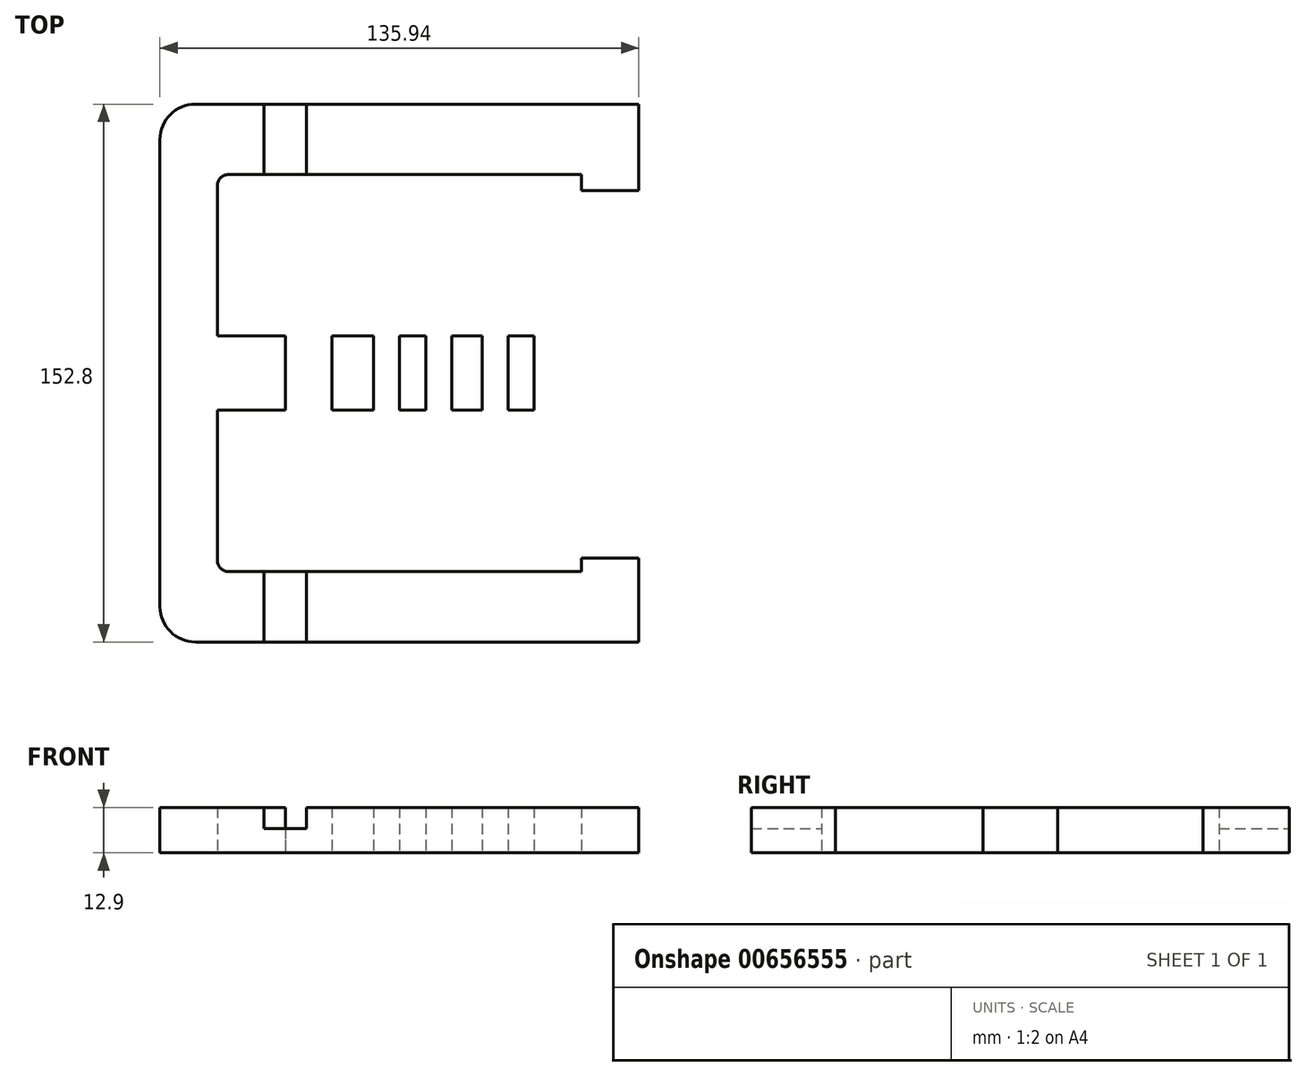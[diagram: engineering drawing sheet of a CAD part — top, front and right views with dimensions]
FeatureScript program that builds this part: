
annotation { "Feature Type Name" : "Feature", "Feature Type Description" : "" }
export const myFeature = defineFeature(function(context is Context, id is Id, definition is map)
    precondition{}
    {
        {
            var Q0;
            Q0=qCreatedBy(makeId("Top.planeOp"),FACE);
            var sketch = newSketch(context, id + "F0", { "sketchPlane" : qUnion([Q0])});
            skLineSegment(sketch, "E0.bottom", {"start": v(-57.93, -76.4) * mm, "end": v(67.97, -76.4) * mm});
            skLineSegment(sketch, "E0.top", {"start": v(-57.93, 76.4) * mm, "end": v(67.97, 76.4) * mm});
            skLineSegment(sketch, "E0.left", {"start": v(-67.97, -66.35) * mm, "end": v(-67.97, 66.35) * mm});
            skLineSegment(sketch, "E0.right", {"start": v(67.97, -76.4) * mm, "end": v(67.97, 76.4) * mm});
            skPoint(sketch, "E0.middle", {"position": v(0, 0) * mm});
            skLineSegment(sketch, "E1.bottom", {"start": v(-48.5, -56.4) * mm, "end": v(51.68, -56.4) * mm});
            skLineSegment(sketch, "E1.top", {"start": v(-48.5, 56.4) * mm, "end": v(51.68, 56.4) * mm});
            skLineSegment(sketch, "E1.left", {"start": v(-51.68, -53.23) * mm, "end": v(-51.68, -10.56) * mm});
            skLineSegment(sketch, "E1.right", {"start": v(51.68, -56.4) * mm, "end": v(51.68, -10.56) * mm});
            skLineSegment(sketch, "E2.bottom", {"start": v(-51.68, -10.56) * mm, "end": v(51.68, -10.56) * mm});
            skLineSegment(sketch, "E2.top", {"start": v(-51.68, 10.56) * mm, "end": v(51.68, 10.56) * mm});
            skLineSegment(sketch, "E3.trimOffspring", {"start": v(-51.68, 10.56) * mm, "end": v(-51.68, 53.23) * mm});
            skLineSegment(sketch, "E4.trimOffspring", {"start": v(51.68, 10.56) * mm, "end": v(51.68, 56.4) * mm});
            skLineSegment(sketch, "E5", {"start": v(-38.44, 76.4) * mm, "end": v(-38.44, 56.4) * mm});
            skLineSegment(sketch, "E6", {"start": v(-26.4, 76.4) * mm, "end": v(-26.4, 56.4) * mm});
            skLineSegment(sketch, "E7", {"start": v(-26.4, -56.4) * mm, "end": v(-26.4, -76.4) * mm});
            skLineSegment(sketch, "E8", {"start": v(-38.44, -56.4) * mm, "end": v(-38.44, -76.4) * mm});
            skLineSegment(sketch, "E9", {"start": v(67.97, 51.87) * mm, "end": v(51.68, 51.87) * mm});
            skLineSegment(sketch, "E10", {"start": v(51.68, 51.87) * mm, "end": v(67.97, 51.87) * mm});
            skLineSegment(sketch, "E11", {"start": v(67.97, -52.52) * mm, "end": v(51.68, -52.52) * mm});
            skLineSegment(sketch, "E12.bottom", {"start": v(-32.37, 10.56) * mm, "end": v(-19.14, 10.56) * mm});
            skLineSegment(sketch, "E12.top", {"start": v(-32.37, -10.56) * mm, "end": v(-19.14, -10.56) * mm});
            skLineSegment(sketch, "E12.left", {"start": v(-32.37, 10.56) * mm, "end": v(-32.37, -10.56) * mm});
            skLineSegment(sketch, "E12.right", {"start": v(-19.14, 10.56) * mm, "end": v(-19.14, -10.56) * mm});
            skLineSegment(sketch, "E13.bottom", {"start": v(-7.39, 10.56) * mm, "end": v(0, 10.56) * mm});
            skLineSegment(sketch, "E13.top", {"start": v(-7.39, -10.56) * mm, "end": v(0, -10.56) * mm});
            skLineSegment(sketch, "E13.left", {"start": v(-7.39, 10.56) * mm, "end": v(-7.39, -10.56) * mm});
            skLineSegment(sketch, "E13.right", {"start": v(0, 10.56) * mm, "end": v(0, -10.56) * mm});
            skLineSegment(sketch, "E14.bottom", {"start": v(7.5, 10.56) * mm, "end": v(14.88, 10.56) * mm});
            skLineSegment(sketch, "E14.top", {"start": v(7.5, -10.56) * mm, "end": v(14.88, -10.56) * mm});
            skLineSegment(sketch, "E14.left", {"start": v(7.5, 10.56) * mm, "end": v(7.5, -10.56) * mm});
            skLineSegment(sketch, "E14.right", {"start": v(14.88, 10.56) * mm, "end": v(14.88, -10.56) * mm});
            skLineSegment(sketch, "E15.bottom", {"start": v(23.47, 10.56) * mm, "end": v(30.86, 10.56) * mm});
            skLineSegment(sketch, "E15.top", {"start": v(23.47, -10.56) * mm, "end": v(30.86, -10.56) * mm});
            skLineSegment(sketch, "E15.left", {"start": v(23.47, 10.56) * mm, "end": v(23.47, -10.56) * mm});
            skLineSegment(sketch, "E15.right", {"start": v(30.86, 10.56) * mm, "end": v(30.86, -10.56) * mm});
            skLineSegment(sketch, "E16.bottom", {"start": v(38.24, 10.56) * mm, "end": v(45.28, 10.56) * mm});
            skLineSegment(sketch, "E16.top", {"start": v(38.24, -10.56) * mm, "end": v(45.28, -10.56) * mm});
            skLineSegment(sketch, "E16.left", {"start": v(38.24, 10.56) * mm, "end": v(38.24, -10.56) * mm});
            skLineSegment(sketch, "E16.right", {"start": v(45.28, 10.56) * mm, "end": v(45.28, -10.56) * mm});
            skPoint(sketch, "E17.visualSharp", {"position": v(-51.68, 56.4) * mm});
            skArc(sketch, "E17.filletArc", {"start": v(-48.5, 56.4) * mm, "mid": v(-50.75, 55.47) * mm, "end": v(-51.68, 53.23) * mm});
            skPoint(sketch, "E18.visualSharp", {"position": v(-67.97, 76.4) * mm});
            skArc(sketch, "E18.filletArc", {"start": v(-57.93, 76.4) * mm, "mid": v(-65.03, 73.45) * mm, "end": v(-67.97, 66.35) * mm});
            skPoint(sketch, "E19.visualSharp", {"position": v(-67.97, -76.4) * mm});
            skArc(sketch, "E19.filletArc", {"start": v(-67.97, -66.35) * mm, "mid": v(-65.03, -73.45) * mm, "end": v(-57.93, -76.4) * mm});
            skPoint(sketch, "E20.visualSharp", {"position": v(-51.68, -56.4) * mm});
            skArc(sketch, "E20.filletArc", {"start": v(-51.68, -53.23) * mm, "mid": v(-50.75, -55.47) * mm, "end": v(-48.5, -56.4) * mm});
            skPoint(sketch, "E21.visualSharp", {"position": v(67.97, -76.4) * mm});
            skPoint(sketch, "E22.visualSharp", {"position": v(67.97, 76.4) * mm});
            skSolve(sketch);
        }
        {
            var Q0;
            {var subQ6=sQuery(id+"F0.wireOp",EDGE,"E0.left");Q0=makeQuery(id+"F0.imprint","IMPRINT",FACE,{"disambiguationData":[TD([[makeQuery(id+"F0.imprint","IMPRINT",EDGE,{"derivedFrom":subQ6}),-1.0]])]});}
            var Q1;
            {var subQ4=sQuery(id+"F0.wireOp",EDGE,"E7");Q1=makeQuery(id+"F0.imprint","IMPRINT",FACE,{"disambiguationData":[TD([[makeQuery(id+"F0.imprint","IMPRINT",EDGE,{"derivedFrom":subQ4}),1.0]])]});}
            var Q2;
            {var subQ0=sQuery(id+"F0.wireOp",EDGE,"E12.right");Q2=makeQuery(id+"F0.imprint","IMPRINT",FACE,{"disambiguationData":[TD([[makeQuery(id+"F0.imprint","IMPRINT",EDGE,{"derivedFrom":subQ0}),1.0]])]});}
            var Q3;
            {var subQ0=sQuery(id+"F0.wireOp",EDGE,"E13.right");Q3=makeQuery(id+"F0.imprint","IMPRINT",FACE,{"disambiguationData":[TD([[makeQuery(id+"F0.imprint","IMPRINT",EDGE,{"derivedFrom":subQ0}),1.0]])]});}
            var Q4;
            {var subQ0=sQuery(id+"F0.wireOp",EDGE,"E14.right");Q4=makeQuery(id+"F0.imprint","IMPRINT",FACE,{"disambiguationData":[TD([[makeQuery(id+"F0.imprint","IMPRINT",EDGE,{"derivedFrom":subQ0}),1.0]])]});}
            var Q5;
            {var subQ0=sQuery(id+"F0.wireOp",EDGE,"E15.right");Q5=makeQuery(id+"F0.imprint","IMPRINT",FACE,{"disambiguationData":[TD([[makeQuery(id+"F0.imprint","IMPRINT",EDGE,{"derivedFrom":subQ0}),1.0]])]});}
            var Q6;
            {var subQ7=sQuery(id+"F0.wireOp",EDGE,"E6");Q6=makeQuery(id+"F0.imprint","IMPRINT",FACE,{"disambiguationData":[TD([[makeQuery(id+"F0.imprint","IMPRINT",EDGE,{"derivedFrom":subQ7}),1.0]])]});}
            var Q7;
            {var subQ0=sQuery(id+"F0.wireOp",EDGE,"E5");Q7=makeQuery(id+"F0.imprint","IMPRINT",FACE,{"disambiguationData":[TD([[makeQuery(id+"F0.imprint","IMPRINT",EDGE,{"derivedFrom":subQ0}),1.0]])]});}
            var Q8;
            {var subQ4=sQuery(id+"F0.wireOp",EDGE,"E10");Q8=makeQuery(id+"F0.imprint","IMPRINT",FACE,{"disambiguationData":[TD([[makeQuery(id+"F0.imprint","IMPRINT",EDGE,{"derivedFrom":subQ4}),-1.0]])]});}
            var Q9;
            Q9=makeQuery(id+"F0.imprint","IMPRINT",FACE,{"disambiguationData":[TD([[makeQuery(id+"F0.imprint","IMPRINT",EDGE,{"derivedFrom":sQuery(id+"F0.wireOp",EDGE,"E16.bottom")}),-1.0]])]});
            var Q10;
            Q10=makeQuery(id+"F0.imprint","IMPRINT",FACE,{"disambiguationData":[TD([[makeQuery(id+"F0.imprint","IMPRINT",EDGE,{"derivedFrom":sQuery(id+"F0.wireOp",EDGE,"E15.bottom")}),-1.0]])]});
            var Q11;
            Q11=makeQuery(id+"F0.imprint","IMPRINT",FACE,{"disambiguationData":[TD([[makeQuery(id+"F0.imprint","IMPRINT",EDGE,{"derivedFrom":sQuery(id+"F0.wireOp",EDGE,"E14.bottom")}),-1.0]])]});
            var Q12;
            Q12=makeQuery(id+"F0.imprint","IMPRINT",FACE,{"disambiguationData":[TD([[makeQuery(id+"F0.imprint","IMPRINT",EDGE,{"derivedFrom":sQuery(id+"F0.wireOp",EDGE,"E13.bottom")}),-1.0]])]});
            var Q13;
            Q13=makeQuery(id+"F0.imprint","IMPRINT",FACE,{"disambiguationData":[TD([[makeQuery(id+"F0.imprint","IMPRINT",EDGE,{"derivedFrom":sQuery(id+"F0.wireOp",EDGE,"E12.bottom")}),-1.0]])]});
            var Q14;
            {var subQ0=sQuery(id+"F0.wireOp",EDGE,"E7");Q14=makeQuery(id+"F0.imprint","IMPRINT",FACE,{"disambiguationData":[TD([[makeQuery(id+"F0.imprint","IMPRINT",EDGE,{"derivedFrom":subQ0}),-1.0]])]});}
            extrude(context, id + "F1", {"entities" : qUnion([Q0, Q1, Q2, Q3, Q4, Q5, Q6, Q7, Q8, Q9, Q10, Q11, Q12, Q13, Q14]), "depth" : 6.95 * mm, "offsetDistance" : 25 * mm});
        }
        {
            var Q0;
            {var subQ6=sQuery(id+"F0.wireOp",EDGE,"E0.left");Q0=makeQuery(id+"F0.imprint","IMPRINT",FACE,{"disambiguationData":[TD([[makeQuery(id+"F0.imprint","IMPRINT",EDGE,{"derivedFrom":subQ6}),-1.0]])]});}
            var Q1;
            {var subQ0=sQuery(id+"F0.wireOp",EDGE,"E12.right");Q1=makeQuery(id+"F0.imprint","IMPRINT",FACE,{"disambiguationData":[TD([[makeQuery(id+"F0.imprint","IMPRINT",EDGE,{"derivedFrom":subQ0}),1.0]])]});}
            var Q2;
            {var subQ0=sQuery(id+"F0.wireOp",EDGE,"E13.right");Q2=makeQuery(id+"F0.imprint","IMPRINT",FACE,{"disambiguationData":[TD([[makeQuery(id+"F0.imprint","IMPRINT",EDGE,{"derivedFrom":subQ0}),1.0]])]});}
            var Q3;
            {var subQ0=sQuery(id+"F0.wireOp",EDGE,"E14.right");Q3=makeQuery(id+"F0.imprint","IMPRINT",FACE,{"disambiguationData":[TD([[makeQuery(id+"F0.imprint","IMPRINT",EDGE,{"derivedFrom":subQ0}),1.0]])]});}
            var Q4;
            {var subQ0=sQuery(id+"F0.wireOp",EDGE,"E15.right");Q4=makeQuery(id+"F0.imprint","IMPRINT",FACE,{"disambiguationData":[TD([[makeQuery(id+"F0.imprint","IMPRINT",EDGE,{"derivedFrom":subQ0}),1.0]])]});}
            var Q5;
            {var subQ4=sQuery(id+"F0.wireOp",EDGE,"E7");Q5=makeQuery(id+"F0.imprint","IMPRINT",FACE,{"disambiguationData":[TD([[makeQuery(id+"F0.imprint","IMPRINT",EDGE,{"derivedFrom":subQ4}),1.0]])]});}
            var Q6;
            {var subQ7=sQuery(id+"F0.wireOp",EDGE,"E6");Q6=makeQuery(id+"F0.imprint","IMPRINT",FACE,{"disambiguationData":[TD([[makeQuery(id+"F0.imprint","IMPRINT",EDGE,{"derivedFrom":subQ7}),1.0]])]});}
            extrude(context, id + "F2", {"entities" : qUnion([Q0, Q1, Q2, Q3, Q4, Q5, Q6]), "operationType" : NewBodyOperationType.ADD, "depth" : 12.9 * mm, "offsetDistance" : 25 * mm});
        }
    });
